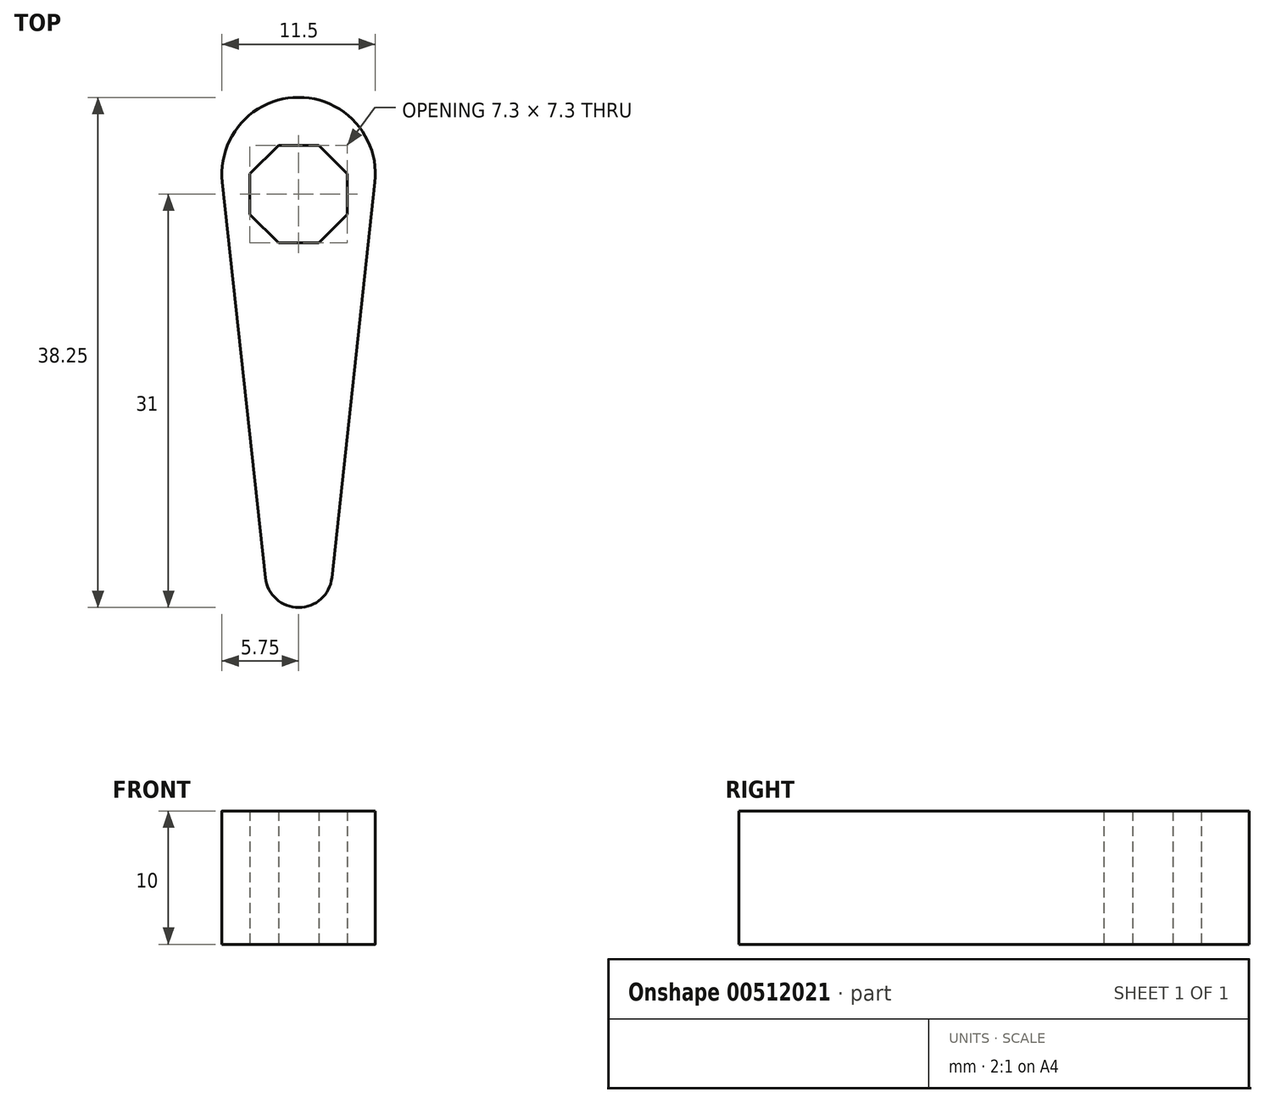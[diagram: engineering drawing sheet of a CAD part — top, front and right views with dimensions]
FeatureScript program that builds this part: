
annotation { "Feature Type Name" : "Feature", "Feature Type Description" : "" }
export const myFeature = defineFeature(function(context is Context, id is Id, definition is map)
    precondition{}
    {
        {
            var Q0;
            Q0=qCreatedBy(makeId("Top.planeOp"),FACE);
            var sketch = newSketch(context, id + "F0", { "sketchPlane" : qUnion([Q0])});
            skCircle(sketch, "E0.cCircle", {"center": v(0, 0) * mm, "radius": 3.65 * mm, "construction": true});
            skLineSegment(sketch, "E0.0", {"start": v(3.65, 1.51) * mm, "end": v(3.65, -1.51) * mm});
            skLineSegment(sketch, "E0.1", {"start": v(3.65, -1.51) * mm, "end": v(1.51, -3.65) * mm});
            skLineSegment(sketch, "E0.2", {"start": v(1.51, -3.65) * mm, "end": v(-1.51, -3.65) * mm});
            skLineSegment(sketch, "E0.3", {"start": v(-1.51, -3.65) * mm, "end": v(-3.65, -1.51) * mm});
            skLineSegment(sketch, "E0.4", {"start": v(-3.65, -1.51) * mm, "end": v(-3.65, 1.51) * mm});
            skLineSegment(sketch, "E0.5", {"start": v(-3.65, 1.51) * mm, "end": v(-1.51, 3.65) * mm});
            skLineSegment(sketch, "E0.6", {"start": v(-1.51, 3.65) * mm, "end": v(1.51, 3.65) * mm});
            skLineSegment(sketch, "E0.7", {"start": v(1.51, 3.65) * mm, "end": v(3.65, 1.51) * mm});
            skPoint(sketch, "E0.0.midPoint", {"position": v(3.65, 0) * mm});
            skArc(sketch, "E1", {"start": v(5.72, 0.88) * mm, "mid": v(0, 7.25) * mm, "end": v(-5.72, 0.88) * mm});
            skArc(sketch, "E2", {"start": v(-2.49, -28.77) * mm, "mid": v(0, -31) * mm, "end": v(2.49, -28.77) * mm});
            skLineSegment(sketch, "E3", {"start": v(-5.72, 0.88) * mm, "end": v(-2.49, -28.77) * mm});
            skLineSegment(sketch, "E4", {"start": v(2.49, -28.77) * mm, "end": v(5.72, 0.88) * mm});
            skCircle(sketch, "E5", {"center": v(0, 0) * mm, "radius": 3.95 * mm, "construction": true});
            skSolve(sketch);
        }
        {
            var Q0;
            Q0 = qSketchRegion(id + "F0", true);
            extrude(context, id + "F1", {"entities" : qUnion([Q0]), "depth" : 10 * mm, "offsetDistance" : 25 * mm, "symmetric" : true});
        }
    });
